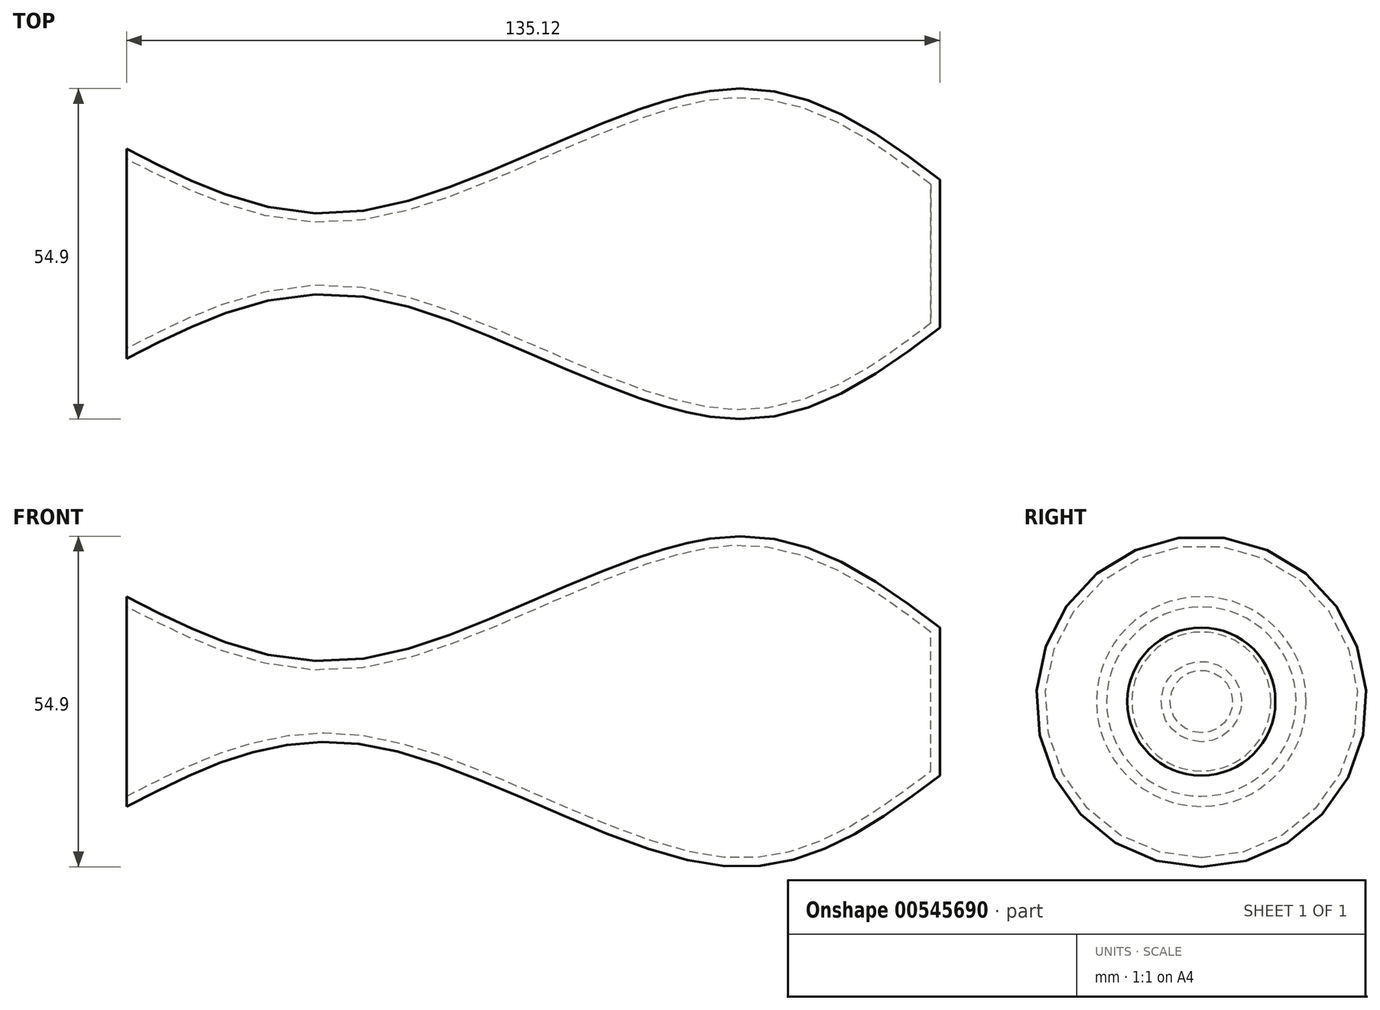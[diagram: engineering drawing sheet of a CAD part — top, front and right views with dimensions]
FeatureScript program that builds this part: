
annotation { "Feature Type Name" : "Feature", "Feature Type Description" : "" }
export const myFeature = defineFeature(function(context is Context, id is Id, definition is map)
    precondition{}
    {
        {
            var Q0;
            Q0=qCreatedBy(makeId("Front.planeOp"),FACE);
            var sketch = newSketch(context, id + "F0", { "sketchPlane" : qUnion([Q0])});
            skFitSpline(sketch, "E0", {"points": [v(-65.74, 17.42) * mm, v(-26.23, 7.17) * mm, v(34.1, 27.37) * mm, v(69.38, 12.3) * mm], "startDerivative": vector(117.7, -60.46) * mm, "endDerivative": vector(106.15, -79.87) * mm});
            skLineSegment(sketch, "E1", {"start": v(69.38, 12.3) * mm, "end": v(69.38, 0) * mm});
            skLineSegment(sketch, "E2", {"start": v(69.38, 0) * mm, "end": v(-65.74, 0) * mm});
            skLineSegment(sketch, "E3", {"start": v(-65.74, 0) * mm, "end": v(-65.74, 17.42) * mm});
            skSolve(sketch);
        }
        {
            var Q0;
            Q0 = qSketchRegion(id + "F0", true);
            var Q1;
            Q1=sQuery(id+"F0.wireOp",EDGE,"E2");
            revolve(context, id + "F1", {"entities" : qUnion([Q0]), "axis" : qUnion([Q1]), "revolveType" : RevolveType.FULL});
        }
        {
            var Q0;
            Q0=makeQuery(id+"F1.opRevolve","SWEPT_FACE",FACE,{"disambiguationData":[OSD([sQuery(id+"F0.wireOp",EDGE,"E3")])]});
            shell(context, id + "F2", {"entities" : qUnion([Q0]), "thickness" : 1.5 * mm});
        }
    });
